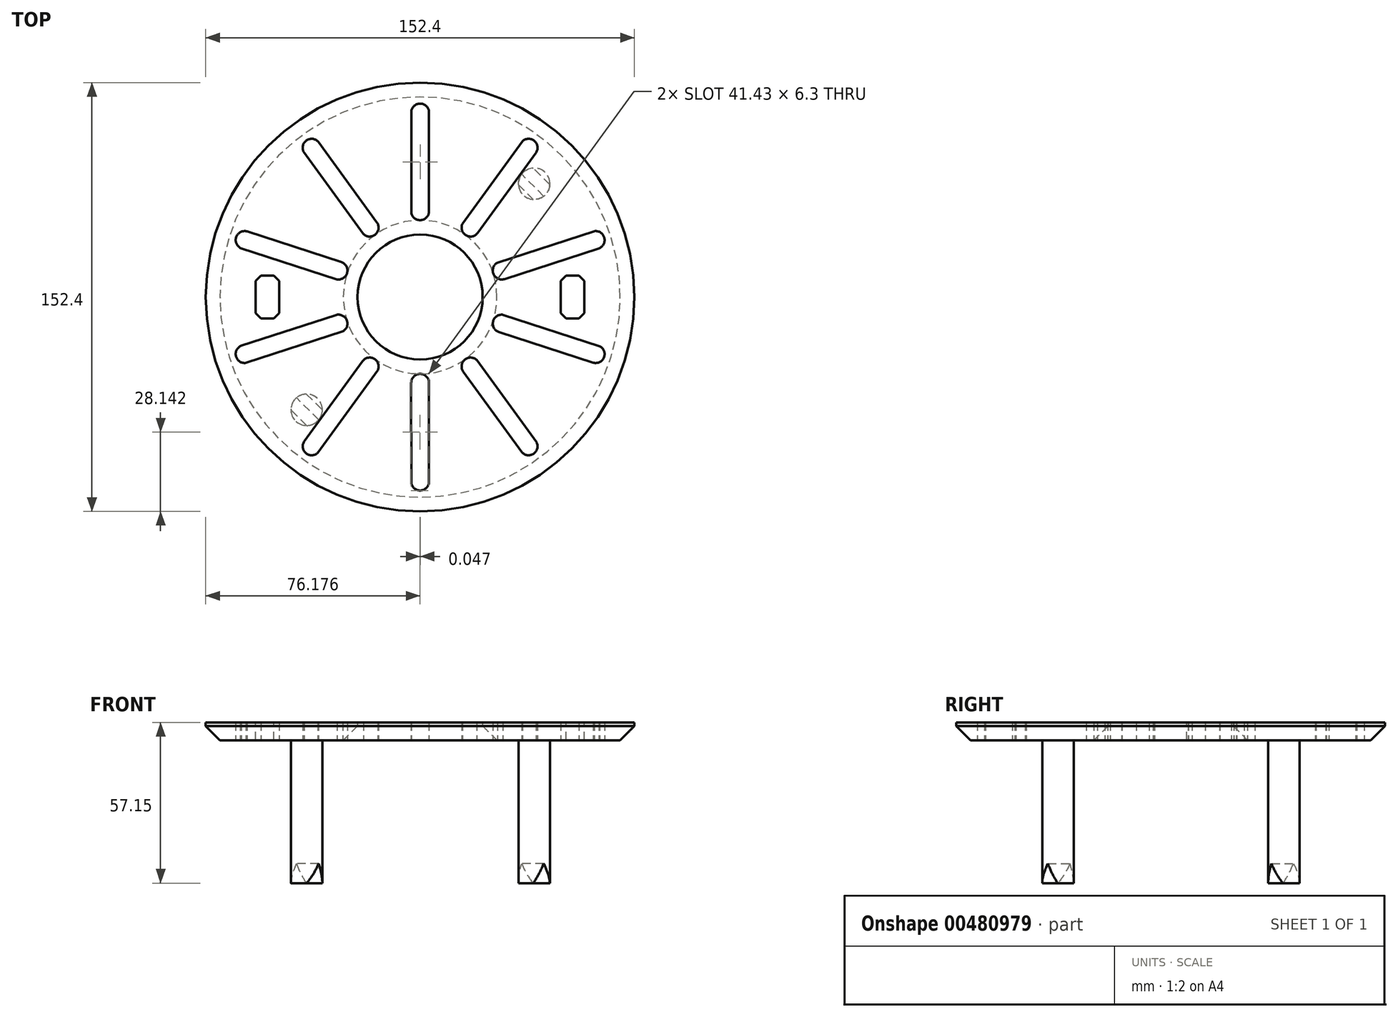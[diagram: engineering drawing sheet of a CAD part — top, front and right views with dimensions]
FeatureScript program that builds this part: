
annotation { "Feature Type Name" : "Feature", "Feature Type Description" : "" }
export const myFeature = defineFeature(function(context is Context, id is Id, definition is map)
    precondition{}
    {
        {
            var Q0;
            Q0=qCreatedBy(makeId("Top.planeOp"),FACE);
            var sketch = newSketch(context, id + "F0", { "sketchPlane" : qUnion([Q0])});
            skCircle(sketch, "E0", {"center": v(0, 0) * mm, "radius": 76.2 * mm});
            skLineSegment(sketch, "E1", {"start": v(76.2, 0) * mm, "end": v(58.42, 0) * mm});
            skLineSegment(sketch, "E2", {"start": v(58.42, 0) * mm, "end": v(58.42, 7.62) * mm});
            skLineSegment(sketch, "E3", {"start": v(58.42, 0) * mm, "end": v(58.42, -7.62) * mm});
            skLineSegment(sketch, "E4", {"start": v(58.42, -7.62) * mm, "end": v(50.04, -7.62) * mm});
            skLineSegment(sketch, "E5", {"start": v(50.04, -7.62) * mm, "end": v(50.04, 7.62) * mm});
            skLineSegment(sketch, "E6", {"start": v(50.04, 7.62) * mm, "end": v(58.42, 7.62) * mm});
            skLineSegment(sketch, "E7", {"start": v(0, 0) * mm, "end": v(0, -8.79) * mm});
            skLineSegment(sketch, "E8.MirrorCS", {"start": v(-50.04, 7.62) * mm, "end": v(-58.42, 7.62) * mm});
            skLineSegment(sketch, "E9.MirrorCS", {"start": v(-76.2, 0) * mm, "end": v(-58.42, 0) * mm});
            skLineSegment(sketch, "E10.MirrorCS", {"start": v(-58.42, 0) * mm, "end": v(-58.42, 7.62) * mm});
            skLineSegment(sketch, "E11.MirrorCS", {"start": v(-58.42, 0) * mm, "end": v(-58.42, -7.62) * mm});
            skLineSegment(sketch, "E12.MirrorCS", {"start": v(-58.42, -7.62) * mm, "end": v(-50.04, -7.62) * mm});
            skLineSegment(sketch, "E13.MirrorCS", {"start": v(-50.04, -7.62) * mm, "end": v(-50.04, 7.62) * mm});
            skCircle(sketch, "E14", {"center": v(0, 0) * mm, "radius": 22.23 * mm});
            skArc(sketch, "E15", {"start": v(-3.13, 29.96) * mm, "mid": v(0.27, 27.35) * mm, "end": v(3.17, 30.5) * mm});
            skArc(sketch, "E16", {"start": v(3.17, 65.79) * mm, "mid": v(0.18, 68.77) * mm, "end": v(-3.13, 66.15) * mm});
            skLineSegment(sketch, "E17", {"start": v(3.17, 65.79) * mm, "end": v(3.17, 30.5) * mm});
            skLineSegment(sketch, "E18", {"start": v(-3.13, 66.15) * mm, "end": v(-3.13, 29.96) * mm});
            skLineSegment(sketch, "E19.1.0", {"start": v(-36.1, 55.09) * mm, "end": v(-15.36, 26.55) * mm});
            skLineSegment(sketch, "E19.1.1", {"start": v(-41.41, 51.68) * mm, "end": v(-20.14, 22.4) * mm});
            skArc(sketch, "E19.1.2", {"start": v(-36.1, 55.09) * mm, "mid": v(-40.28, 55.74) * mm, "end": v(-41.41, 51.68) * mm});
            skArc(sketch, "E19.1.3", {"start": v(-20.14, 22.4) * mm, "mid": v(-15.85, 22.28) * mm, "end": v(-15.36, 26.55) * mm});
            skLineSegment(sketch, "E19.2.0", {"start": v(-61.59, 23.34) * mm, "end": v(-28.03, 12.45) * mm});
            skLineSegment(sketch, "E19.2.1", {"start": v(-63.88, 17.47) * mm, "end": v(-29.46, 6.28) * mm});
            skArc(sketch, "E19.2.2", {"start": v(-61.59, 23.34) * mm, "mid": v(-65.35, 21.42) * mm, "end": v(-63.88, 17.47) * mm});
            skArc(sketch, "E19.2.3", {"start": v(-29.46, 6.28) * mm, "mid": v(-25.92, 8.71) * mm, "end": v(-28.03, 12.45) * mm});
            skLineSegment(sketch, "E19.3.0", {"start": v(-63.55, -17.31) * mm, "end": v(-30, -6.4) * mm});
            skLineSegment(sketch, "E19.3.1", {"start": v(-61.94, -23.42) * mm, "end": v(-27.53, -12.23) * mm});
            skArc(sketch, "E19.3.2", {"start": v(-63.55, -17.31) * mm, "mid": v(-65.46, -21.08) * mm, "end": v(-61.94, -23.42) * mm});
            skArc(sketch, "E19.3.3", {"start": v(-27.53, -12.23) * mm, "mid": v(-26.1, -8.19) * mm, "end": v(-30, -6.4) * mm});
            skLineSegment(sketch, "E19.4.0", {"start": v(-41.23, -51.36) * mm, "end": v(-20.5, -22.82) * mm});
            skLineSegment(sketch, "E19.4.1", {"start": v(-36.35, -55.35) * mm, "end": v(-15.08, -26.08) * mm});
            skArc(sketch, "E19.4.2", {"start": v(-41.23, -51.36) * mm, "mid": v(-40.57, -55.53) * mm, "end": v(-36.35, -55.35) * mm});
            skArc(sketch, "E19.4.3", {"start": v(-15.08, -26.08) * mm, "mid": v(-16.3, -21.96) * mm, "end": v(-20.5, -22.82) * mm});
            skLineSegment(sketch, "E19.5.0", {"start": v(-3.17, -65.79) * mm, "end": v(-3.17, -30.5) * mm});
            skLineSegment(sketch, "E19.5.1", {"start": v(3.13, -66.15) * mm, "end": v(3.13, -29.96) * mm});
            skArc(sketch, "E19.5.2", {"start": v(-3.17, -65.79) * mm, "mid": v(-0.18, -68.77) * mm, "end": v(3.13, -66.15) * mm});
            skArc(sketch, "E19.5.3", {"start": v(3.13, -29.96) * mm, "mid": v(-0.27, -27.35) * mm, "end": v(-3.17, -30.5) * mm});
            skLineSegment(sketch, "E19.6.0", {"start": v(36.1, -55.09) * mm, "end": v(15.36, -26.55) * mm});
            skLineSegment(sketch, "E19.6.1", {"start": v(41.41, -51.68) * mm, "end": v(20.14, -22.4) * mm});
            skArc(sketch, "E19.6.2", {"start": v(36.1, -55.09) * mm, "mid": v(40.28, -55.74) * mm, "end": v(41.41, -51.68) * mm});
            skArc(sketch, "E19.6.3", {"start": v(20.14, -22.4) * mm, "mid": v(15.85, -22.28) * mm, "end": v(15.36, -26.55) * mm});
            skLineSegment(sketch, "E19.7.0", {"start": v(61.59, -23.34) * mm, "end": v(28.03, -12.45) * mm});
            skLineSegment(sketch, "E19.7.1", {"start": v(63.88, -17.47) * mm, "end": v(29.46, -6.28) * mm});
            skArc(sketch, "E19.7.2", {"start": v(61.59, -23.34) * mm, "mid": v(65.35, -21.42) * mm, "end": v(63.88, -17.47) * mm});
            skArc(sketch, "E19.7.3", {"start": v(29.46, -6.28) * mm, "mid": v(25.92, -8.71) * mm, "end": v(28.03, -12.45) * mm});
            skLineSegment(sketch, "E19.8.0", {"start": v(63.55, 17.31) * mm, "end": v(30, 6.4) * mm});
            skLineSegment(sketch, "E19.8.1", {"start": v(61.94, 23.42) * mm, "end": v(27.53, 12.23) * mm});
            skArc(sketch, "E19.8.2", {"start": v(63.55, 17.31) * mm, "mid": v(65.46, 21.08) * mm, "end": v(61.94, 23.42) * mm});
            skArc(sketch, "E19.8.3", {"start": v(27.53, 12.23) * mm, "mid": v(26.1, 8.19) * mm, "end": v(30, 6.4) * mm});
            skLineSegment(sketch, "E19.9.0", {"start": v(41.23, 51.36) * mm, "end": v(20.5, 22.82) * mm});
            skLineSegment(sketch, "E19.9.1", {"start": v(36.35, 55.35) * mm, "end": v(15.08, 26.08) * mm});
            skArc(sketch, "E19.9.2", {"start": v(41.23, 51.36) * mm, "mid": v(40.57, 55.53) * mm, "end": v(36.35, 55.35) * mm});
            skArc(sketch, "E19.9.3", {"start": v(15.08, 26.08) * mm, "mid": v(16.3, 21.96) * mm, "end": v(20.5, 22.82) * mm});
            skSolve(sketch);
        }
        {
            var Q0;
            Q0 = qSketchRegion(id + "F0", true);
            extrude(context, id + "F1", {"entities" : qUnion([Q0]), "depth" : 6.35 * mm});
        }
        {
            var Q0;
            Q0=makeQuery(id+"F1.opExtrude","SWEPT_EDGE",EDGE,{"disambiguationData":[OSD([sQuery(id+"F0.wireOp",EDGE,"E2"),sQuery(id+"F0.wireOp",EDGE,"E6")])]});
            var Q1;
            Q1=makeQuery(id+"F1.opExtrude","SWEPT_EDGE",EDGE,{"disambiguationData":[OSD([sQuery(id+"F0.wireOp",EDGE,"E5"),sQuery(id+"F0.wireOp",EDGE,"E6")])]});
            var Q2;
            Q2=makeQuery(id+"F1.opExtrude","SWEPT_EDGE",EDGE,{"disambiguationData":[OSD([sQuery(id+"F0.wireOp",EDGE,"E3"),sQuery(id+"F0.wireOp",EDGE,"E4")])]});
            var Q3;
            Q3=makeQuery(id+"F1.opExtrude","SWEPT_EDGE",EDGE,{"disambiguationData":[OSD([sQuery(id+"F0.wireOp",EDGE,"E4"),sQuery(id+"F0.wireOp",EDGE,"E5")])]});
            var Q4;
            Q4=makeQuery(id+"F1.opExtrude","SWEPT_EDGE",EDGE,{"disambiguationData":[OSD([sQuery(id+"F0.wireOp",EDGE,"E8.MirrorCS"),sQuery(id+"F0.wireOp",EDGE,"E13.MirrorCS")])]});
            var Q5;
            Q5=makeQuery(id+"F1.opExtrude","SWEPT_EDGE",EDGE,{"disambiguationData":[OSD([sQuery(id+"F0.wireOp",EDGE,"E8.MirrorCS"),sQuery(id+"F0.wireOp",EDGE,"E10.MirrorCS")])]});
            var Q6;
            Q6=makeQuery(id+"F1.opExtrude","SWEPT_EDGE",EDGE,{"disambiguationData":[OSD([sQuery(id+"F0.wireOp",EDGE,"E12.MirrorCS"),sQuery(id+"F0.wireOp",EDGE,"E13.MirrorCS")])]});
            var Q7;
            Q7=makeQuery(id+"F1.opExtrude","SWEPT_EDGE",EDGE,{"disambiguationData":[OSD([sQuery(id+"F0.wireOp",EDGE,"E11.MirrorCS"),sQuery(id+"F0.wireOp",EDGE,"E12.MirrorCS")])]});
            chamfer(context, id + "F2", {"entities" : qUnion([Q0, Q1, Q2, Q3, Q4, Q5, Q6, Q7]), "width" : 1.9 * mm, "tangentPropagation" : true});
        }
        {
            var Q0;
            Q0=makeQuery(id+"F1.opExtrude","CAP_FACE",FACE,{"disambiguationData":[OSD([sQuery(id+"F0.wireOp",EDGE,"E0"),sQuery(id+"F0.wireOp",EDGE,"E2"),sQuery(id+"F0.wireOp",EDGE,"E3"),sQuery(id+"F0.wireOp",EDGE,"E4"),sQuery(id+"F0.wireOp",EDGE,"E5"),sQuery(id+"F0.wireOp",EDGE,"E6"),sQuery(id+"F0.wireOp",EDGE,"E8.MirrorCS"),sQuery(id+"F0.wireOp",EDGE,"E10.MirrorCS"),sQuery(id+"F0.wireOp",EDGE,"E11.MirrorCS"),sQuery(id+"F0.wireOp",EDGE,"E12.MirrorCS"),sQuery(id+"F0.wireOp",EDGE,"E13.MirrorCS"),sQuery(id+"F0.wireOp",EDGE,"E14")])],"isStart":true});
            var sketch = newSketch(context, id + "F3", { "sketchPlane" : qUnion([Q0])});
            skCircle(sketch, "E20", {"center": v(0, 0) * mm, "radius": 57.15 * mm});
            skCircle(sketch, "E21", {"center": v(40.55, -40.28) * mm, "radius": 5.59 * mm});
            skCircle(sketch, "E22.MirrorC", {"center": v(-40.35, 40.09) * mm, "radius": 5.59 * mm});
            skLineSegment(sketch, "E23", {"start": v(0, 0) * mm, "end": v(76.2, 0) * mm});
            skLineSegment(sketch, "E24", {"start": v(0, 0) * mm, "end": v(66.55, -66.55) * mm});
            skLineSegment(sketch, "E25", {"start": v(0, 0) * mm, "end": v(-65.6, 65.17) * mm});
            skSolve(sketch);
        }
        {
            var Q0;
            {var subQ0=sQuery(id+"F3.wireOp",EDGE,"E22.MirrorC");var subQ1=sQuery(id+"F3.wireOp",EDGE,"E20");var subQ2=makeQuery(id+"F3.imprint","INTERSECT",VERTEX,{"disambiguationData":[OD(0.0)],"derivedFrom":[subQ1,subQ0]});Q0=makeQuery(id+"F3.imprint","IMPRINT",FACE,{"disambiguationData":[TD([[makeQuery(id+"F3.imprint","IMPRINT",EDGE,{"disambiguationData":[TD([[subQ2,-1.0]])],"derivedFrom":subQ1}),-1.0]])]});}
            var Q1;
            {var subQ0=sQuery(id+"F3.wireOp",EDGE,"E22.MirrorC");var subQ1=sQuery(id+"F3.wireOp",EDGE,"E20");var subQ2=makeQuery(id+"F3.imprint","INTERSECT",VERTEX,{"disambiguationData":[OD(0.0)],"derivedFrom":[subQ1,subQ0]});Q1=makeQuery(id+"F3.imprint","IMPRINT",FACE,{"disambiguationData":[TD([[makeQuery(id+"F3.imprint","IMPRINT",EDGE,{"disambiguationData":[TD([[subQ2,-1.0]])],"derivedFrom":subQ1}),1.0]])]});}
            var Q2;
            {var subQ0=sQuery(id+"F3.wireOp",EDGE,"E21");var subQ1=sQuery(id+"F3.wireOp",EDGE,"E20");var subQ2=makeQuery(id+"F3.imprint","INTERSECT",VERTEX,{"disambiguationData":[OD(0.0)],"derivedFrom":[subQ1,subQ0]});Q2=makeQuery(id+"F3.imprint","IMPRINT",FACE,{"disambiguationData":[TD([[makeQuery(id+"F3.imprint","IMPRINT",EDGE,{"disambiguationData":[TD([[subQ2,-1.0]])],"derivedFrom":subQ1}),1.0]])]});}
            var Q3;
            {var subQ0=sQuery(id+"F3.wireOp",EDGE,"E21");var subQ1=sQuery(id+"F3.wireOp",EDGE,"E20");var subQ2=makeQuery(id+"F3.imprint","INTERSECT",VERTEX,{"disambiguationData":[OD(0.0)],"derivedFrom":[subQ1,subQ0]});Q3=makeQuery(id+"F3.imprint","IMPRINT",FACE,{"disambiguationData":[TD([[makeQuery(id+"F3.imprint","IMPRINT",EDGE,{"disambiguationData":[TD([[subQ2,-1.0]])],"derivedFrom":subQ1}),-1.0]])]});}
            var Q4;
            {var subQ0=sQuery(id+"F3.wireOp",EDGE,"E25");var subQ1=sQuery(id+"F3.wireOp",EDGE,"E20");var subQ2=makeQuery(id+"F3.imprint","INTERSECT",VERTEX,{"derivedFrom":[subQ1,subQ0]});Q4=makeQuery(id+"F3.imprint","IMPRINT",FACE,{"disambiguationData":[TD([[makeQuery(id+"F3.imprint","IMPRINT",EDGE,{"disambiguationData":[TD([[subQ2,-1.0]])],"derivedFrom":subQ1}),1.0]])]});}
            var Q5;
            {var subQ0=sQuery(id+"F3.wireOp",EDGE,"E25");var subQ1=sQuery(id+"F3.wireOp",EDGE,"E20");var subQ2=makeQuery(id+"F3.imprint","INTERSECT",VERTEX,{"derivedFrom":[subQ1,subQ0]});Q5=makeQuery(id+"F3.imprint","IMPRINT",FACE,{"disambiguationData":[TD([[makeQuery(id+"F3.imprint","IMPRINT",EDGE,{"disambiguationData":[TD([[subQ2,-1.0]])],"derivedFrom":subQ1}),-1.0]])]});}
            var Q6;
            {var subQ0=sQuery(id+"F3.wireOp",EDGE,"E24");var subQ1=sQuery(id+"F3.wireOp",EDGE,"E20");var subQ2=makeQuery(id+"F3.imprint","INTERSECT",VERTEX,{"derivedFrom":[subQ1,subQ0]});Q6=makeQuery(id+"F3.imprint","IMPRINT",FACE,{"disambiguationData":[TD([[makeQuery(id+"F3.imprint","IMPRINT",EDGE,{"disambiguationData":[TD([[subQ2,-1.0]])],"derivedFrom":subQ1}),-1.0]])]});}
            var Q7;
            {var subQ0=sQuery(id+"F3.wireOp",EDGE,"E24");var subQ1=sQuery(id+"F3.wireOp",EDGE,"E20");var subQ2=makeQuery(id+"F3.imprint","INTERSECT",VERTEX,{"derivedFrom":[subQ1,subQ0]});Q7=makeQuery(id+"F3.imprint","IMPRINT",FACE,{"disambiguationData":[TD([[makeQuery(id+"F3.imprint","IMPRINT",EDGE,{"disambiguationData":[TD([[subQ2,-1.0]])],"derivedFrom":subQ1}),1.0]])]});}
            extrude(context, id + "F4", {"entities" : qUnion([Q0, Q1, Q2, Q3, Q4, Q5, Q6, Q7]), "operationType" : NewBodyOperationType.ADD, "depth" : 50.8 * mm});
        }
        {
            var Q0;
            Q0=makeQuery(id+"F1.opExtrude","CAP_FACE",FACE,{"disambiguationData":[OSD([sQuery(id+"F0.wireOp",EDGE,"E0"),sQuery(id+"F0.wireOp",EDGE,"E2"),sQuery(id+"F0.wireOp",EDGE,"E3"),sQuery(id+"F0.wireOp",EDGE,"E4"),sQuery(id+"F0.wireOp",EDGE,"E5"),sQuery(id+"F0.wireOp",EDGE,"E6"),sQuery(id+"F0.wireOp",EDGE,"E8.MirrorCS"),sQuery(id+"F0.wireOp",EDGE,"E10.MirrorCS"),sQuery(id+"F0.wireOp",EDGE,"E11.MirrorCS"),sQuery(id+"F0.wireOp",EDGE,"E12.MirrorCS"),sQuery(id+"F0.wireOp",EDGE,"E13.MirrorCS"),sQuery(id+"F0.wireOp",EDGE,"E14")])],"isStart":false});
            var sketch = newSketch(context, id + "F5", { "sketchPlane" : qUnion([Q0])});
            skLineSegment(sketch, "E26", {"start": v(0, 0) * mm, "end": v(53.88, 53.88) * mm});
            skSolve(sketch);
        }
        {
            var Q0;
            Q0=qCreatedBy(makeId("Front.planeOp"),FACE);
            var Q1;
            Q1=sQuery(id+"F5.wireOp",EDGE,"E26");
            cPlane(context, id + "F6", {"entities" : qUnion([Q0, Q1]), "cplaneType" : CPlaneType.LINE_ANGLE, "offset" : 25.4 * mm, "angle" : 0 * degree, "width" : 152.4 * mm, "height" : 152.4 * mm});
        }
        {
            var Q0;
            Q0=qCreatedBy(id+"F6.planeOp",FACE);
            var sketch = newSketch(context, id + "F7", { "sketchPlane" : qUnion([Q0])});
            skLineSegment(sketch, "E27", {"start": v(62.01, -52.64) * mm, "end": v(56.38, -43.8) * mm});
            skLineSegment(sketch, "E28", {"start": v(56.38, -43.8) * mm, "end": v(51.38, -54.04) * mm});
            skLineSegment(sketch, "E29", {"start": v(51.38, -54.04) * mm, "end": v(62.01, -54.04) * mm});
            skLineSegment(sketch, "E30", {"start": v(0, 0) * mm, "end": v(0, -20.11) * mm});
            skLineSegment(sketch, "E31.MirrorCS", {"start": v(-56.38, -43.8) * mm, "end": v(-51.38, -54.04) * mm});
            skLineSegment(sketch, "E32.MirrorCS", {"start": v(-62.01, -52.64) * mm, "end": v(-56.38, -43.8) * mm});
            skLineSegment(sketch, "E33.MirrorCS", {"start": v(-51.38, -54.04) * mm, "end": v(-62.01, -54.04) * mm});
            skLineSegment(sketch, "E34", {"start": v(62.01, -52.64) * mm, "end": v(62.01, -54.04) * mm});
            skLineSegment(sketch, "E35", {"start": v(-62.01, -52.64) * mm, "end": v(-62.01, -54.04) * mm});
            skSolve(sketch);
        }
        {
            var Q0;
            Q0 = qSketchRegion(id + "F7", true);
            extrude(context, id + "F8", {"entities" : qUnion([Q0]), "operationType" : NewBodyOperationType.REMOVE, "oppositeDirection" : true, "depth" : 25.4 * mm, "hasSecondDirection" : true, "secondDirectionOppositeDirection" : false, "secondDirectionDepth" : 25.4 * mm});
        }
        {
            var Q0;
            Q0=makeQuery(id+"F1.opExtrude","CAP_EDGE",EDGE,{"disambiguationData":[OSD([sQuery(id+"F0.wireOp",EDGE,"E0")])],"isStart":true});
            chamfer(context, id + "F9", {"entities" : qUnion([Q0]), "width" : 5.08 * mm, "tangentPropagation" : true});
        }
        {
            var Q0;
            Q0=makeQuery(id+"F1.opExtrude","CAP_EDGE",EDGE,{"disambiguationData":[OSD([sQuery(id+"F0.wireOp",EDGE,"E14")])],"isStart":true});
            chamfer(context, id + "F10", {"entities" : qUnion([Q0]), "width" : 5.08 * mm, "tangentPropagation" : true});
        }
    });
